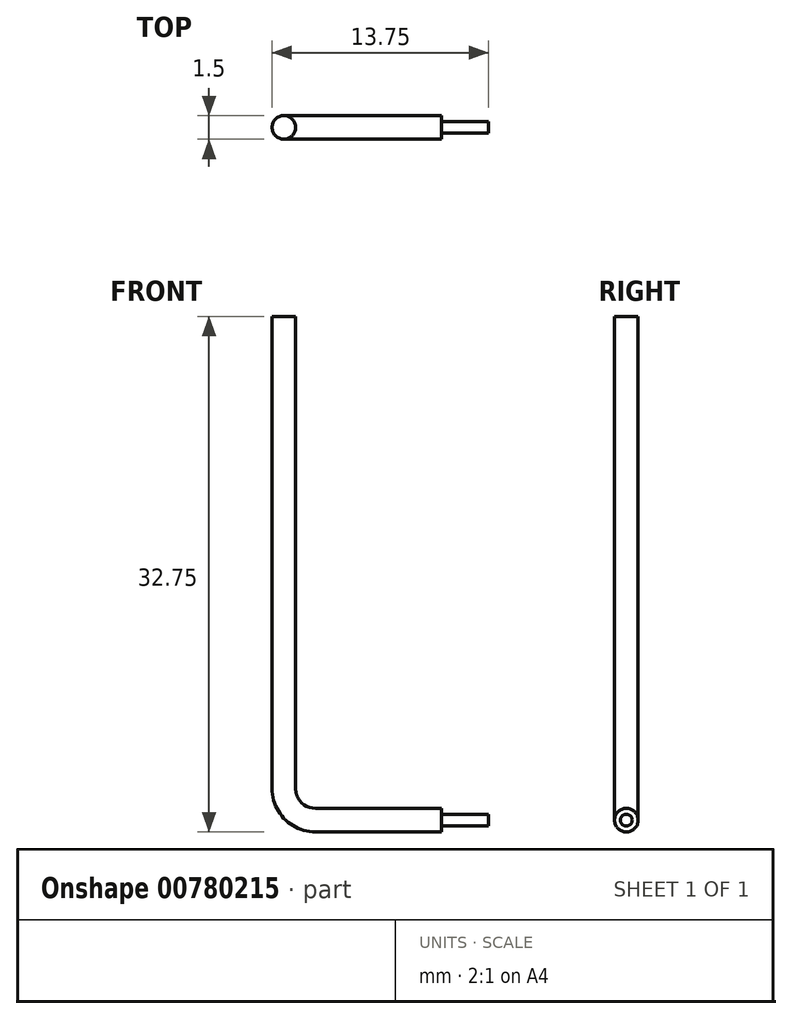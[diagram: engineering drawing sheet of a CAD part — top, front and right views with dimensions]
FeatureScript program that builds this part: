
annotation { "Feature Type Name" : "Feature", "Feature Type Description" : "" }
export const myFeature = defineFeature(function(context is Context, id is Id, definition is map)
    precondition{}
    {
        {
            var Q0;
            Q0=qCreatedBy(makeId("Front.planeOp"),FACE);
            var sketch = newSketch(context, id + "F0", { "sketchPlane" : qUnion([Q0])});
            skLineSegment(sketch, "E0", {"start": v(0, 2) * mm, "end": v(0, 30) * mm});
            skLineSegment(sketch, "E1", {"start": v(2, 0) * mm, "end": v(10, 0) * mm});
            skPoint(sketch, "E2.visualSharp", {"position": v(0, 32) * mm});
            skPoint(sketch, "E3.visualSharp", {"position": v(0, 0) * mm});
            skArc(sketch, "E3.filletArc", {"start": v(0, 2) * mm, "mid": v(0.59, 0.59) * mm, "end": v(2, 0) * mm});
            skLineSegment(sketch, "E4", {"start": v(0, 30) * mm, "end": v(0, 32) * mm});
            skSolve(sketch);
        }
        {
            var Q0;
            Q0=qCreatedBy(makeId("Right.planeOp"),FACE);
            cPlane(context, id + "F1", {"entities" : qUnion([Q0]), "cplaneType" : CPlaneType.OFFSET, "offset" : 10 * mm, "width" : 150 * mm, "height" : 150 * mm});
        }
        {
            var Q0;
            Q0=qCreatedBy(id+"F1.planeOp",FACE);
            var sketch = newSketch(context, id + "F2", { "sketchPlane" : qUnion([Q0])});
            skCircle(sketch, "E5", {"center": v(0, 0) * mm, "radius": 0.38 * mm});
            skCircle(sketch, "E6", {"center": v(0, 0) * mm, "radius": 0.75 * mm});
            skSolve(sketch);
        }
        {
            var Q0;
            Q0 = qSketchRegion(id + "F2", true);
            var Q1;
            Q1=makeQuery(id+"F2.imprint","IMPRINT",FACE,{"disambiguationData":[TD([[makeQuery(id+"F2.imprint","IMPRINT",EDGE,{"derivedFrom":sQuery(id+"F2.wireOp",EDGE,"E5")}),1.0]])]});
            var Q2;
            Q2=sQuery(id+"F0.wireOp",EDGE,"E1");
            var Q3;
            Q3=sQuery(id+"F0.wireOp",EDGE,"E3.filletArc");
            var Q4;
            Q4=sQuery(id+"F0.wireOp",EDGE,"E0");
            var Q5;
            Q5=sQuery(id+"F0.wireOp",EDGE,"E2.filletArc");
            var Q6;
            Q6=sQuery(id+"F0.wireOp",EDGE,"E4");
            sweep(context, id + "F3", {"profiles" : qUnion([Q0, Q1]), "path" : qUnion([Q2, Q3, Q4, Q5, Q6])});
        }
        {
            var Q0;
            Q0=makeQuery(id+"F2.imprint","IMPRINT",FACE,{"disambiguationData":[TD([[makeQuery(id+"F2.imprint","IMPRINT",EDGE,{"derivedFrom":sQuery(id+"F2.wireOp",EDGE,"E5")}),1.0]])]});
            extrude(context, id + "F4", {"entities" : qUnion([Q0]), "operationType" : NewBodyOperationType.ADD, "depth" : 3 * mm, "offsetDistance" : 25 * mm});
        }
    });
